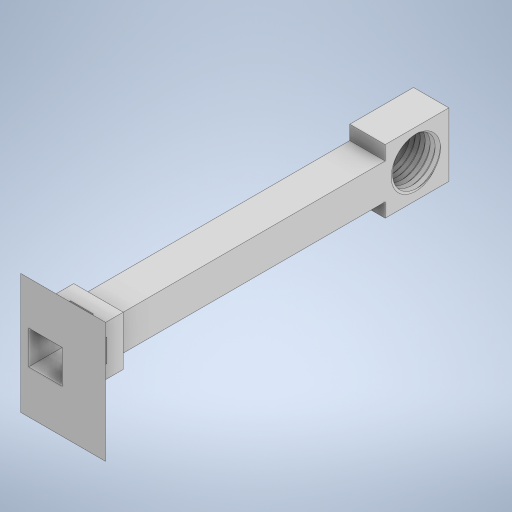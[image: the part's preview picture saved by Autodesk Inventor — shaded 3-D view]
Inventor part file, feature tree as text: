
AUTODESK INVENTOR PART (.ipt)
format: ipt  version: 2024 (Build 280153000, 153)  size: 558,592 bytes
history: native  units: mm
features: sketch x16, extrude x15, mirror x2, other x1
ambient origin geometry x8: Origin, YZ Plane, XZ Plane, XY Plane, X Axis, Y Axis, Z Axis, Center Point
bodies: Volumenkörper1 (feature_tree)
feature tree (34):
  extrude  "Extrusion1"  Depth=10.0mm
  extrude  "Extrusion2"  Depth=10.0mm
  extrude  "Extrusion3"  Depth=18.0mm TaperAngle=0.0deg
  extrude  "Extrusion4"  Depth=9.0mm TaperAngle=0.0deg
  other  "Spirale1"
  extrude  "Extrusion6"  Depth=9.0mm TaperAngle=0.0deg
  extrude  "Extrusion12"  Depth=10.0mm
  mirror  "Spiegeln1"
  extrude  "Extrusion13"  Depth=0.2mm
  mirror  "Spiegeln2"
  extrude  "Extrusion7"  Depth=9.5mm
  extrude  "Extrusion8"  Depth=9.75mm TaperAngle=0.0deg
  extrude  "Extrusion9"  Depth=1.5mm
  extrude  "Extrusion14"  Depth=5.0mm
  extrude  "Extrusion15"  Depth=1.5mm
  extrude  "Extrusion16"  Depth=1.5mm
  extrude  "Extrusion17"  Depth=5.0mm
  extrude  "Extrusion18"  Depth=2.0mm TaperAngle=0.0deg
  sketch  "Skizze1"  dims[d0=10.0mm d1=10.0mm]
  sketch  "Skizze2"  dims[d2=91.0mm d3=0.0mm d4=10.0mm]
  sketch  "Skizze3"  dims[d5=18.0mm d6=18.0mm d7=0.0mm]
  sketch  "Skizze4"  dims[d8=15.0mm d9=9.0mm d10=0.0mm]
  sketch  "Skizze5"  dims[d17=12.2mm d18=9.0mm d19=0.0mm]
  sketch  "Skizze7"  dims[d22=1.4mm d23=11.0mm d24=10.0mm d25=0.0mm d26=90.0deg d27=90.0deg d28=0.0mm d29=0.0mm d33=1.7mm]
  sketch  "Skizze8"  dims[d34=60.0deg d35=0.2mm]
  sketch  "Skizze9"  dims[d36=1.0mm d37=0.0mm d39=9.5mm]
  sketch  "Skizze10"  dims[d40=9.5mm d41=9.75mm d42=0.0mm]
  sketch  "Skizze16"  dims[d43=1.5mm d44=1.5mm]
  sketch  "Skizze17"  dims[d45=5.0mm d46=5.0mm]
  sketch  "Skizze18"  dims[d47=1.5mm d48=1.5mm]
  sketch  "Skizze20"  dims[d49=1.5mm d50=1.5mm]
  sketch  "Skizze22"  dims[d51=5.0mm d52=5.0mm]
  sketch  "Skizze23"  dims[d53=1.2mm d54=0.0mm d55=2.0mm d56=0.0mm]
  sketch  "Skizze24"  dims[d65=10.0mm d66=15.0mm d67=2.0mm d68=0.0mm d69=2.0mm d70=0.0mm d71=10.0mm d72=0.0mm d73=10.0mm d74=7.0mm d75=10.0mm d76=24.0mm d77=0.0mm d78=10.0mm d79=24.0mm d80=0.0mm d81=24.0mm d82=0.0mm d83=60.0mm d84=0.0mm d85=10.0mm d86=0.0mm d38=0.0mm]
